# Revit family: FU_Modular_Sandler_Escala_ESC0435LC
name_source: partatom
category: Furniture
units: mm (PartAtom-declared; Revit-internal decimal feet)

## family parameters
Always vertical = Yes
Cut with Voids When Loaded = No
OmniClass Number = 23.40.20.00
OmniClass Title = General Furniture and Specialties
Room Calculation Point = No
Shared = No
Work Plane-Based = No

## types (1)
- Escalas 0430LC
    Default Elevation = 0 mm  [stored 0 ft]
    Depth = 800 mm  [stored 2.62467 ft]
    Description = 40cm right arm-table with an oak table top and upholstered arm.
    Height = 590 mm  [stored 1.9357 ft]
    Manufacturer = Sandler
    Model = Escalas 0435LC
    Seat Material = Fabric - Mainline Flax - Upminster MLF20
    URL = https://www.sandlerseating.com
    Width = 400 mm  [stored 1.31234 ft]

note: [stored X ft] marks values corroborated as IEEE doubles in the binary element streams (Revit-internal decimal feet)

## geometry (parser evidence)
native form markers: Sweep x2
no freeform markers — native parametric forms only
